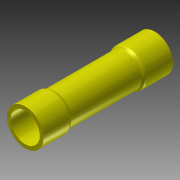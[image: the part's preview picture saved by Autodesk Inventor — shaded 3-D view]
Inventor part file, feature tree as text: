
AUTODESK INVENTOR PART (.ipt)
format: ipt  version: 2014 (Build 180170000, 170)  size: 182,272 bytes
history: native  units: in
note: dims shown in document units (in); Inventor stores cm internally (conversion verified against a paired STEP export)
features: sketch x3, extrude x2, fillet x2, projected_geometry x2, mirror x1, shell x1, revolve x1, chamfer x1
ambient origin geometry x8: Origin, YZ Plane, XZ Plane, XY Plane, X Axis, Y Axis, Z Axis, Center Point
bodies: Solid1 (feature_tree), Solid2 (feature_tree)
feature tree (13):
  extrude  "Extrusion1"  Depth=0.9735in TaperAngle=0.0deg
  extrude  "Extrusion2"  Depth=0.03in TaperAngle=0.0deg
  fillet  "Fillet1"  Radius=0.01in
  fillet  "Fillet2"  Radius=0.03in
  mirror  "Mirror1"
  shell  "Shell1"  Thickness=0.0275in
  revolve  "Revolution1"  [1 undecoded]
  chamfer  "Chamfer1"  Distance=0.03in
  sketch  "Sketch1"  dims[d0=0.2465in d1=0.9735in d2=0.0in]
  sketch  "Sketch2"  dims[d3=0.274in d4=0.215in d5=0.0in d6=0.01in d7=0.03in d8=0.0275in]
  projected_geometry  "Projected Loop1"
  sketch  "Sketch3"  dims[d9=0.0145in d10=0.03in d11=0.03in d12=90.0deg d13=0.008in d14=0.125in d15=45.0deg]
  projected_geometry  "Project Cut Edges1"
note: 1 required parameter value undecoded (feature->parameter linkage not recoverable at this tier; creation-order binding heuristic only, values carry confidence <= 0.55)
